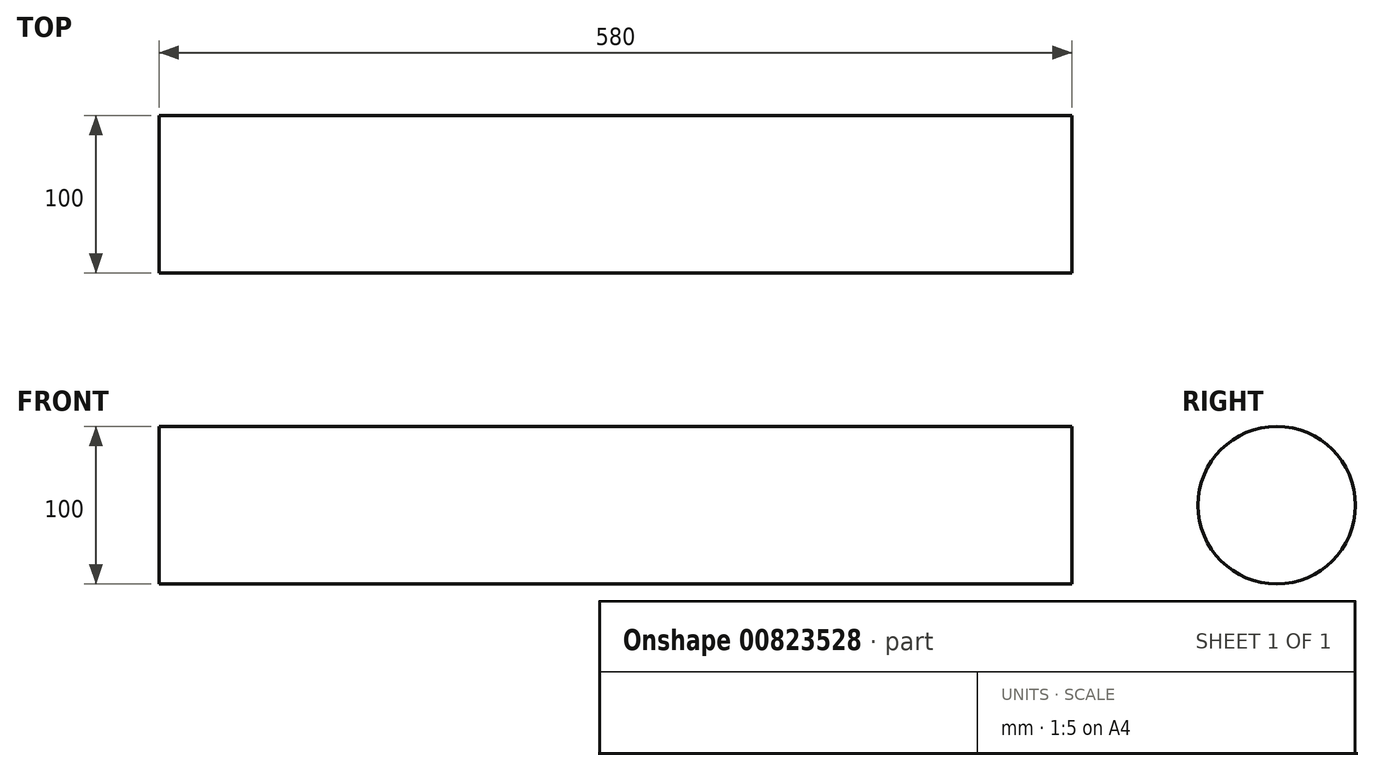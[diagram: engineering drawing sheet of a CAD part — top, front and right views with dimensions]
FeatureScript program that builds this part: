
annotation { "Feature Type Name" : "Feature", "Feature Type Description" : "" }
export const myFeature = defineFeature(function(context is Context, id is Id, definition is map)
    precondition{}
    {
        {
            var Q0;
            Q0=qCreatedBy(makeId("Right.planeOp"),FACE);
            var sketch = newSketch(context, id + "F0", { "sketchPlane" : qUnion([Q0])});
            skCircle(sketch, "E0", {"center": v(0, 0) * mm, "radius": 50 * mm});
            skSolve(sketch);
        }
        {
            var Q0;
            Q0=makeQuery(id+"F0.imprint","IMPRINT",FACE,{"disambiguationData":[TD([[makeQuery(id+"F0.imprint","IMPRINT",EDGE,{"derivedFrom":sQuery(id+"F0.wireOp",EDGE,"E0")}),1.0]])]});
            extrude(context, id + "F1", {"entities" : qUnion([Q0]), "depth" : 580 * mm, "offsetDistance" : 25 * mm});
        }
    });
